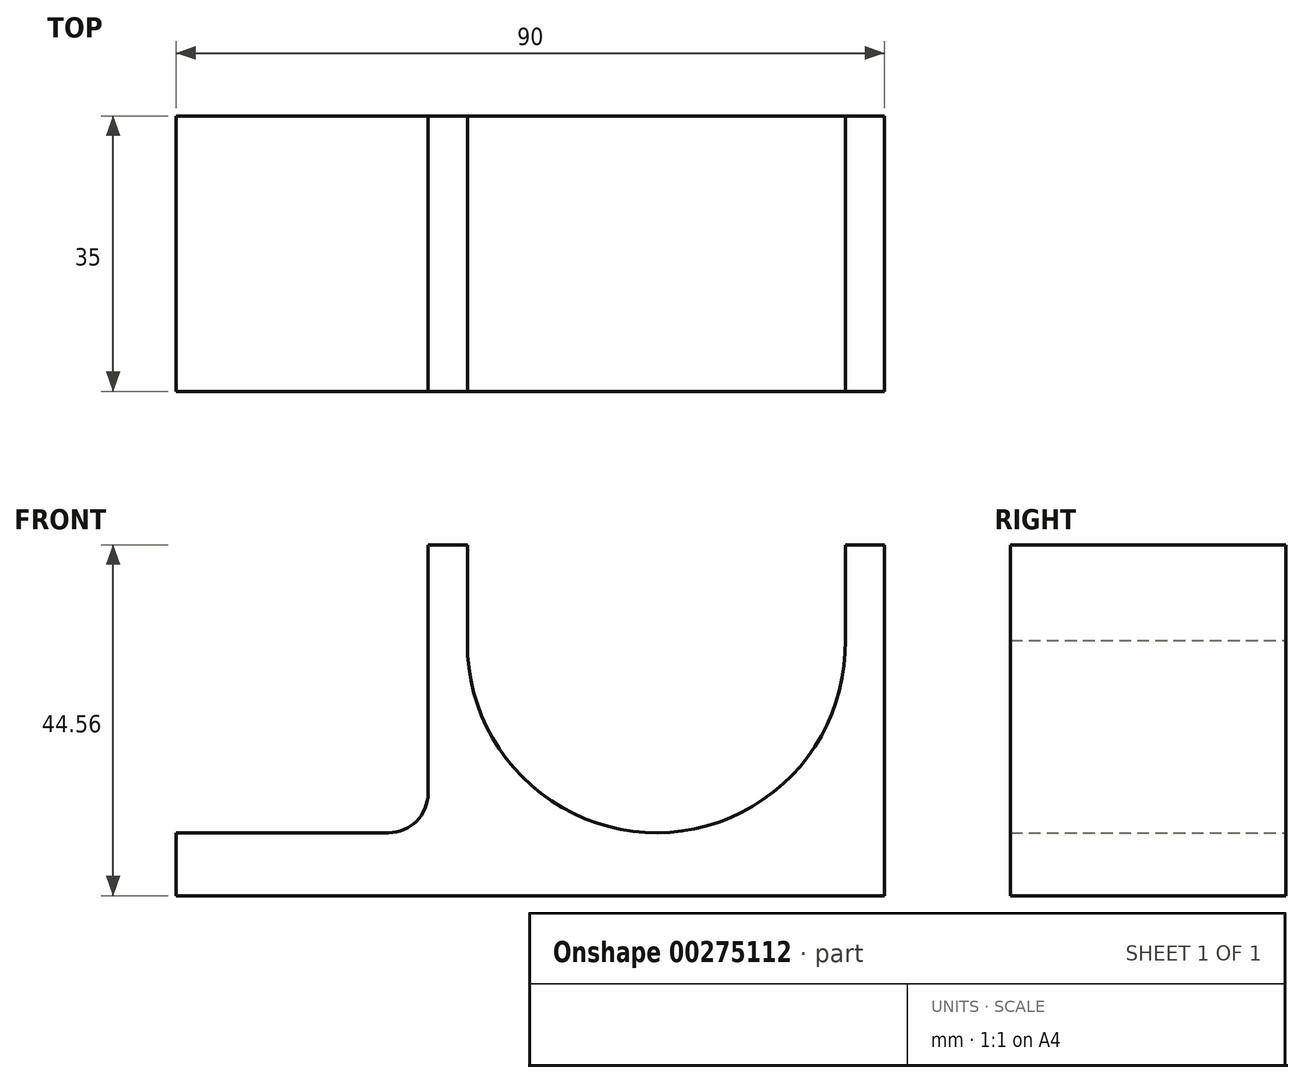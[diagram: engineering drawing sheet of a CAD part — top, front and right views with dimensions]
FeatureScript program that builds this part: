
annotation { "Feature Type Name" : "Feature", "Feature Type Description" : "" }
export const myFeature = defineFeature(function(context is Context, id is Id, definition is map)
    precondition{}
    {
        {
            var Q0;
            Q0=qCreatedBy(makeId("Front.planeOp"),FACE);
            var sketch = newSketch(context, id + "F0", { "sketchPlane" : qUnion([Q0])});
            skLineSegment(sketch, "E0", {"start": v(-32.43, -8.2) * mm, "end": v(-32.43, -16.2) * mm});
            skLineSegment(sketch, "E1", {"start": v(-32.43, -16.2) * mm, "end": v(57.57, -16.2) * mm});
            skLineSegment(sketch, "E2", {"start": v(57.57, -16.2) * mm, "end": v(57.57, 28.37) * mm});
            skLineSegment(sketch, "E3", {"start": v(57.57, 28.37) * mm, "end": v(-0.43, 28.37) * mm});
            skLineSegment(sketch, "E4", {"start": v(-0.43, 28.37) * mm, "end": v(-0.43, -3.2) * mm});
            skLineSegment(sketch, "E5", {"start": v(-5.43, -8.2) * mm, "end": v(-32.43, -8.2) * mm});
            skCircle(sketch, "E6", {"center": v(28.57, 15.8) * mm, "radius": 24 * mm});
            skLineSegment(sketch, "E7.bottom", {"start": v(4.57, 15.66) * mm, "end": v(13.53, 15.66) * mm});
            skLineSegment(sketch, "E7.top", {"start": v(4.57, 49.43) * mm, "end": v(13.53, 49.43) * mm});
            skLineSegment(sketch, "E7.left", {"start": v(4.57, 15.66) * mm, "end": v(4.57, 49.43) * mm});
            skLineSegment(sketch, "E7.right", {"start": v(13.53, 15.66) * mm, "end": v(13.53, 49.43) * mm});
            skLineSegment(sketch, "E8.bottom", {"start": v(52.57, 16.26) * mm, "end": v(43.6, 16.26) * mm});
            skLineSegment(sketch, "E8.top", {"start": v(52.57, 51.6) * mm, "end": v(43.6, 51.6) * mm});
            skLineSegment(sketch, "E8.left", {"start": v(52.57, 16.26) * mm, "end": v(52.57, 51.6) * mm});
            skLineSegment(sketch, "E8.right", {"start": v(43.6, 16.26) * mm, "end": v(43.6, 51.6) * mm});
            skPoint(sketch, "E9.visualSharp", {"position": v(-0.43, -8.2) * mm});
            skArc(sketch, "E9.filletArc", {"start": v(-5.43, -8.2) * mm, "mid": v(-1.9, -6.73) * mm, "end": v(-0.43, -3.2) * mm});
            skSolve(sketch);
        }
        {
            var Q0;
            Q0=makeQuery(id+"F0.imprint","IMPRINT",FACE,{"disambiguationData":[TD([[makeQuery(id+"F0.imprint","IMPRINT",EDGE,{"derivedFrom":sQuery(id+"F0.wireOp",EDGE,"E0")}),1.0]])]});
            extrude(context, id + "F1", {"entities" : qUnion([Q0]), "depth" : 25 * mm});
        }
        {
            var Q0;
            Q0=makeQuery(id+"F1.opExtrude","CAP_FACE",FACE,{"disambiguationData":[OSD([sQuery(id+"F0.wireOp",EDGE,"E0"),sQuery(id+"F0.wireOp",EDGE,"E1"),sQuery(id+"F0.wireOp",EDGE,"E2"),sQuery(id+"F0.wireOp",EDGE,"E3"),sQuery(id+"F0.wireOp",EDGE,"E4"),sQuery(id+"F0.wireOp",EDGE,"E5"),sQuery(id+"F0.wireOp",EDGE,"E6"),sQuery(id+"F0.wireOp",EDGE,"E7.left"),sQuery(id+"F0.wireOp",EDGE,"E8.left"),sQuery(id+"F0.wireOp",EDGE,"E9.filletArc")])],"isStart":false});
            extrude(context, id + "F2", {"entities" : qUnion([Q0]), "operationType" : NewBodyOperationType.ADD, "depth" : 10 * mm});
        }
    });
